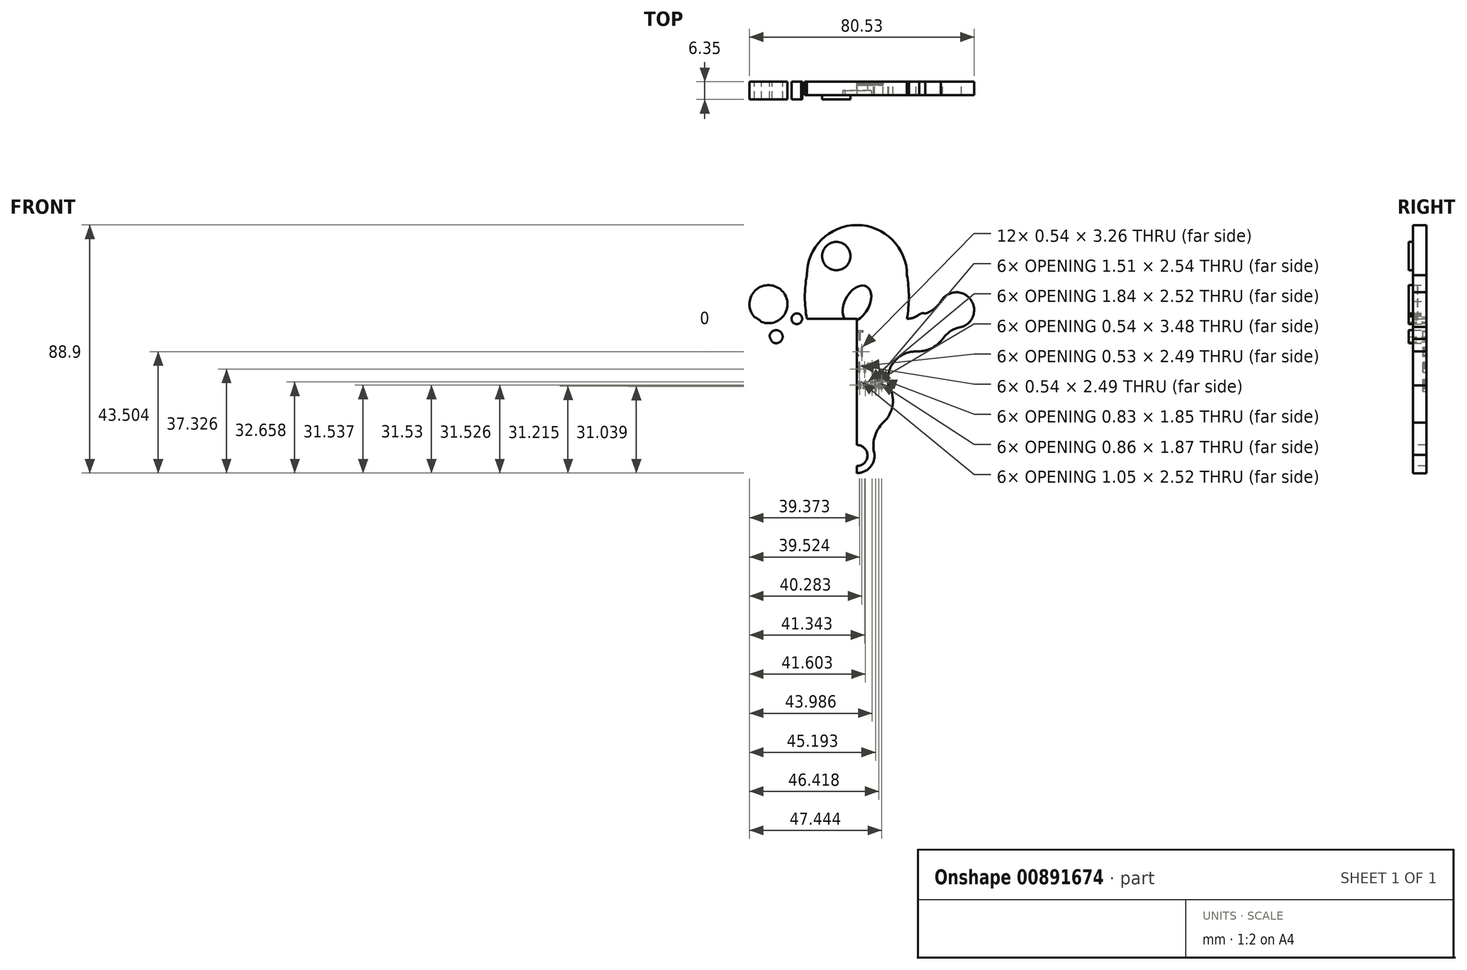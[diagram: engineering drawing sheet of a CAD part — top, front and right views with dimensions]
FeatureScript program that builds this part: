
annotation { "Feature Type Name" : "Feature", "Feature Type Description" : "" }
export const myFeature = defineFeature(function(context is Context, id is Id, definition is map)
    precondition{}
    {
        {
            var Q0;
            Q0=qCreatedBy(makeId("Front.planeOp"),FACE);
            var sketch = newSketch(context, id + "F0", { "sketchPlane" : qUnion([Q0])});
            skLineSegment(sketch, "E0.bottom", {"start": v(-17.94, 11.59) * mm, "end": v(17.94, 11.59) * mm});
            skLineSegment(sketch, "E0.top", {"start": v(-17.94, 27.23) * mm, "end": v(17.94, 27.23) * mm});
            skPoint(sketch, "E0.middle", {"position": v(0, 19.41) * mm});
            skArc(sketch, "E1", {"start": v(17.94, 27.23) * mm, "mid": v(0, 45.18) * mm, "end": v(-17.94, 27.23) * mm});
            skLineSegment(sketch, "E2", {"start": v(-17.94, 11.59) * mm, "end": v(0, 11.59) * mm});
            skLineSegment(sketch, "E3", {"start": v(0, 11.59) * mm, "end": v(0, -27.44) * mm});
            skLineSegment(sketch, "E4", {"start": v(0, -27.44) * mm, "end": v(0, -34) * mm});
            skCircle(sketch, "E5", {"center": v(-31.7, 16.82) * mm, "radius": 6.82 * mm});
            skCircle(sketch, "E6", {"center": v(35.65, 14.71) * mm, "radius": 6.36 * mm});
            skCircle(sketch, "E7", {"center": v(0, -37.4) * mm, "radius": 6.33 * mm});
            skCircle(sketch, "E8", {"center": v(-28.95, 5.17) * mm, "radius": 2.34 * mm});
            skCircle(sketch, "E9", {"center": v(-21.53, 11.59) * mm, "radius": 1.9 * mm});
            skArc(sketch, "E10", {"start": v(-19.98, 12.7) * mm, "mid": v(-19.1, 11.88) * mm, "end": v(-17.94, 11.59) * mm});
            skArc(sketch, "E11", {"start": v(-25.07, 18.4) * mm, "mid": v(-23.74, 15.74) * mm, "end": v(-21.82, 13.47) * mm});
            skArc(sketch, "E12", {"start": v(-6.2, -36.14) * mm, "mid": v(-8.21, -28.4) * mm, "end": v(-14.49, -23.44) * mm});
            skArc(sketch, "E13", {"start": v(-31.29, 5.17) * mm, "mid": v(-29.02, 1.8) * mm, "end": v(-25.38, 0) * mm});
            skPoint(sketch, "E14.startSnap0", {"position": v(10.2, -17.56) * mm});
            skArc(sketch, "E15", {"start": v(21.15, -0.12) * mm, "mid": v(13.28, -3.81) * mm, "end": v(11.38, -12.3) * mm});
            skArc(sketch, "E16", {"start": v(21.15, -0.12) * mm, "mid": v(26.51, 0.92) * mm, "end": v(30.77, 4.35) * mm});
            skCircle(sketch, "E17", {"center": v(23.71, 11.2) * mm, "radius": 2.37 * mm});
            skArc(sketch, "E18", {"start": v(24.52, 13.44) * mm, "mid": v(27.64, 15.17) * mm, "end": v(30.08, 17.78) * mm});
            skArc(sketch, "E19", {"start": v(17.94, 11.59) * mm, "mid": v(20.27, 11.99) * mm, "end": v(22.33, 13.14) * mm});
            skArc(sketch, "E20", {"start": v(37.47, 8.62) * mm, "mid": v(33.64, 7.23) * mm, "end": v(30.77, 4.35) * mm});
            skArc(sketch, "E21", {"start": v(-17.94, 27.23) * mm, "mid": v(-18.64, 19.41) * mm, "end": v(-17.94, 11.59) * mm});
            skArc(sketch, "E22", {"start": v(17.94, 11.59) * mm, "mid": v(18.6, 19.41) * mm, "end": v(17.94, 27.23) * mm});
            skArc(sketch, "E23", {"start": v(-20.49, -14.03) * mm, "mid": v(-19.15, -19.8) * mm, "end": v(-14.49, -23.44) * mm});
            skArc(sketch, "E24", {"start": v(-20.49, -14.03) * mm, "mid": v(-19.5, -5.82) * mm, "end": v(-25.38, 0) * mm});
            skArc(sketch, "E25", {"start": v(-31.29, 5.17) * mm, "mid": v(-33.14, 9.34) * mm, "end": v(-36.7, 12.19) * mm});
            skArc(sketch, "E26", {"start": v(9.44, -25.57) * mm, "mid": v(12.8, -19.28) * mm, "end": v(11.38, -12.3) * mm});
            skArc(sketch, "E27", {"start": v(9.44, -25.57) * mm, "mid": v(6.3, -30.92) * mm, "end": v(6.33, -37.12) * mm});
            skLineSegment(sketch, "E28", {"start": v(0, 45.18) * mm, "end": v(0, -43.72) * mm});
            skSolve(sketch);
        }
        {
            var Q0;
            Q0=makeQuery(id+"F0.imprint","IMPRINT",FACE,{"disambiguationData":[TD([[makeQuery(id+"F0.imprint","IMPRINT",EDGE,{"derivedFrom":sQuery(id+"F0.wireOp",EDGE,"E0.top")}),1.0]])]});
            var Q1;
            Q1=makeQuery(id+"F0.imprint","IMPRINT",FACE,{"disambiguationData":[TD([[makeQuery(id+"F0.imprint","IMPRINT",EDGE,{"derivedFrom":sQuery(id+"F0.wireOp",EDGE,"E0.bottom")}),1.0]])]});
            var Q2;
            {var subQ3=sQuery(id+"F0.wireOp",EDGE,"E2");Q2=makeQuery(id+"F0.imprint","IMPRINT",FACE,{"disambiguationData":[TD([[makeQuery(id+"F0.imprint","IMPRINT",EDGE,{"derivedFrom":subQ3}),-1.0]])]});}
            var Q3;
            {var subQ0=sQuery(id+"F0.wireOp",EDGE,"E5");var subQ1=makeQuery(id+"F0.imprint","INTERSECT",VERTEX,{"derivedFrom":[subQ0,sQuery(id+"F0.wireOp",EDGE,"E11")]});Q3=makeQuery(id+"F0.imprint","IMPRINT",FACE,{"disambiguationData":[TD([[makeQuery(id+"F0.imprint","IMPRINT",EDGE,{"disambiguationData":[TD([[subQ1,-1.0]])],"derivedFrom":subQ0}),1.0]])]});}
            var Q4;
            {var subQ12=sQuery(id+"F0.wireOp",EDGE,"E0.bottom");Q4=makeQuery(id+"F0.imprint","IMPRINT",FACE,{"disambiguationData":[TD([[makeQuery(id+"F0.imprint","IMPRINT",EDGE,{"derivedFrom":subQ12}),-1.0]])]});}
            var Q5;
            {var subQ0=sQuery(id+"F0.wireOp",EDGE,"E6");var subQ1=makeQuery(id+"F0.imprint","INTERSECT",VERTEX,{"derivedFrom":[subQ0,sQuery(id+"F0.wireOp",EDGE,"E18")]});Q5=makeQuery(id+"F0.imprint","IMPRINT",FACE,{"disambiguationData":[TD([[makeQuery(id+"F0.imprint","IMPRINT",EDGE,{"disambiguationData":[TD([[subQ1,-1.0]])],"derivedFrom":subQ0}),1.0]])]});}
            var Q6;
            {var subQ0=sQuery(id+"F0.wireOp",EDGE,"E17");var subQ1=makeQuery(id+"F0.imprint","INTERSECT",VERTEX,{"derivedFrom":[subQ0,sQuery(id+"F0.wireOp",EDGE,"E18")]});Q6=makeQuery(id+"F0.imprint","IMPRINT",FACE,{"disambiguationData":[TD([[makeQuery(id+"F0.imprint","IMPRINT",EDGE,{"disambiguationData":[TD([[subQ1,-1.0]])],"derivedFrom":subQ0}),1.0]])]});}
            var Q7;
            {var subQ0=sQuery(id+"F0.wireOp",EDGE,"E10");var subQ1=sQuery(id+"F0.wireOp",EDGE,"E9");var subQ2=makeQuery(id+"F0.imprint","INTERSECT",VERTEX,{"disambiguationData":[OD(0.0)],"derivedFrom":[subQ1,subQ0]});Q7=makeQuery(id+"F0.imprint","IMPRINT",FACE,{"disambiguationData":[TD([[makeQuery(id+"F0.imprint","IMPRINT",EDGE,{"disambiguationData":[TD([[subQ2,-1.0]])],"derivedFrom":subQ1}),1.0]])]});}
            var Q8;
            {var subQ0=sQuery(id+"F0.wireOp",EDGE,"E13");var subQ1=sQuery(id+"F0.wireOp",EDGE,"E8");var subQ3=makeQuery(id+"F0.imprint","INTERSECT",VERTEX,{"derivedFrom":[subQ1,subQ0]});Q8=makeQuery(id+"F0.imprint","IMPRINT",FACE,{"disambiguationData":[TD([[makeQuery(id+"F0.imprint","IMPRINT",EDGE,{"disambiguationData":[TD([[subQ3,-1.0]])],"derivedFrom":subQ1}),1.0]])]});}
            var Q9;
            {var subQ0=sQuery(id+"F0.wireOp",EDGE,"E7");var subQ1=makeQuery(id+"F0.imprint","INTERSECT",VERTEX,{"derivedFrom":[sQuery(id+"F0.wireOp",EDGE,"E4"),subQ0]});Q9=makeQuery(id+"F0.imprint","IMPRINT",FACE,{"disambiguationData":[TD([[makeQuery(id+"F0.imprint","IMPRINT",EDGE,{"disambiguationData":[TD([[subQ1,1.0]])],"derivedFrom":subQ0}),1.0]])]});}
            var Q10;
            {var subQ0=sQuery(id+"F0.wireOp",EDGE,"E28");var subQ1=makeQuery(id+"F0.imprint","IMPRINT",VERTEX,{"derivedFrom":subQ0});Q10=makeQuery(id+"F0.imprint","IMPRINT",FACE,{"disambiguationData":[TD([[makeQuery(id+"F0.imprint","IMPRINT",EDGE,{"disambiguationData":[TD([[subQ1,1.0]])],"derivedFrom":subQ0}),1.0]])]});}
            var Q11;
            {var subQ4=sQuery(id+"F0.wireOp",EDGE,"E2");Q11=makeQuery(id+"F0.imprint","IMPRINT",FACE,{"disambiguationData":[TD([[makeQuery(id+"F0.imprint","IMPRINT",EDGE,{"derivedFrom":subQ4}),1.0]])]});}
            extrude(context, id + "F1", {"entities" : qUnion([Q0, Q1, Q2, Q3, Q4, Q5, Q6, Q7, Q8, Q9, Q10, Q11]), "depth" : 6.35 * mm, "offsetDistance" : 25.4 * mm});
        }
        {
            var Q0;
            Q0=makeQuery(id+"F1.opExtrude","CAP_FACE",FACE,{"disambiguationData":[OSD([sQuery(id+"F0.wireOp",EDGE,"E1"),sQuery(id+"F0.wireOp",EDGE,"E5"),sQuery(id+"F0.wireOp",EDGE,"E6"),sQuery(id+"F0.wireOp",EDGE,"E7"),sQuery(id+"F0.wireOp",EDGE,"E9"),sQuery(id+"F0.wireOp",EDGE,"E10"),sQuery(id+"F0.wireOp",EDGE,"E11"),sQuery(id+"F0.wireOp",EDGE,"E12"),sQuery(id+"F0.wireOp",EDGE,"E13"),sQuery(id+"F0.wireOp",EDGE,"E15"),sQuery(id+"F0.wireOp",EDGE,"E16"),sQuery(id+"F0.wireOp",EDGE,"E17"),sQuery(id+"F0.wireOp",EDGE,"E18"),sQuery(id+"F0.wireOp",EDGE,"E19"),sQuery(id+"F0.wireOp",EDGE,"E20"),sQuery(id+"F0.wireOp",EDGE,"E21"),sQuery(id+"F0.wireOp",EDGE,"E22"),sQuery(id+"F0.wireOp",EDGE,"E23"),sQuery(id+"F0.wireOp",EDGE,"E24"),sQuery(id+"F0.wireOp",EDGE,"E25"),sQuery(id+"F0.wireOp",EDGE,"E26"),sQuery(id+"F0.wireOp",EDGE,"E27")])],"isStart":false});
            var sketch = newSketch(context, id + "F2", { "sketchPlane" : qUnion([Q0])});
            skCircle(sketch, "E29", {"center": v(7.39, 31.47) * mm, "radius": 5.22 * mm});
            skEllipse(sketch, "E30", {"center": v(0, 17.03) * mm, "majorRadius": 7.04 * mm, "minorRadius": 4.37 * mm, "majorAxis": v(-0.5, -0.87)});
            skCircle(sketch, "E31", {"center": v(-7.37, 34.04) * mm, "radius": 5.08 * mm});
            skCircle(sketch, "E32", {"center": v(0, -37.4) * mm, "radius": 3.64 * mm});
            skLineSegment(sketch, "E33", {"start": v(-7.37, 34.04) * mm, "end": v(0, 34.04) * mm});
            skLineSegment(sketch, "E34", {"start": v(7.39, 31.47) * mm, "end": v(0, 31.47) * mm});
            skPoint(sketch, "E34.endSnap0", {"position": v(0, 45.18) * mm});
            skLineSegment(sketch, "E35", {"start": v(0, 34.04) * mm, "end": v(0, 45.18) * mm});
            skLineSegment(sketch, "E36", {"start": v(0, 31.47) * mm, "end": v(0, 45.18) * mm});
            skSolve(sketch);
        }
        {
            var Q0;
            Q0=makeQuery(id+"F2.imprint","IMPRINT",FACE,{"disambiguationData":[TD([[makeQuery(id+"F2.imprint","IMPRINT",EDGE,{"derivedFrom":sQuery(id+"F2.wireOp",EDGE,"E30")}),1.0]])]});
            var Q1;
            Q1=sQuery(id+"F2.wireOp",EDGE,"E30");
            extrude(context, id + "F3", {"entities" : qUnion([Q0]), "operationType" : NewBodyOperationType.REMOVE, "surfaceEntities" : qUnion([Q1]), "oppositeDirection" : true, "depth" : 3.17 * mm, "offsetDistance" : 25.4 * mm});
        }
        {
            var Q0;
            Q0=makeQuery(id+"F1.opExtrude","CAP_FACE",FACE,{"disambiguationData":[OSD([sQuery(id+"F0.wireOp",EDGE,"E1"),sQuery(id+"F0.wireOp",EDGE,"E5"),sQuery(id+"F0.wireOp",EDGE,"E6"),sQuery(id+"F0.wireOp",EDGE,"E7"),sQuery(id+"F0.wireOp",EDGE,"E9"),sQuery(id+"F0.wireOp",EDGE,"E10"),sQuery(id+"F0.wireOp",EDGE,"E11"),sQuery(id+"F0.wireOp",EDGE,"E12"),sQuery(id+"F0.wireOp",EDGE,"E13"),sQuery(id+"F0.wireOp",EDGE,"E15"),sQuery(id+"F0.wireOp",EDGE,"E16"),sQuery(id+"F0.wireOp",EDGE,"E17"),sQuery(id+"F0.wireOp",EDGE,"E18"),sQuery(id+"F0.wireOp",EDGE,"E19"),sQuery(id+"F0.wireOp",EDGE,"E20"),sQuery(id+"F0.wireOp",EDGE,"E21"),sQuery(id+"F0.wireOp",EDGE,"E22"),sQuery(id+"F0.wireOp",EDGE,"E23"),sQuery(id+"F0.wireOp",EDGE,"E24"),sQuery(id+"F0.wireOp",EDGE,"E25"),sQuery(id+"F0.wireOp",EDGE,"E26"),sQuery(id+"F0.wireOp",EDGE,"E27")])],"isStart":false});
            var sketch = newSketch(context, id + "F4", { "sketchPlane" : qUnion([Q0])});
            skLineSegment(sketch, "E37", {"start": v(0, 45.18) * mm, "end": v(0, 34.03) * mm});
            skLineSegment(sketch, "E38", {"start": v(0, 34.03) * mm, "end": v(0, 45.18) * mm});
            skLineSegment(sketch, "E39", {"start": v(0, 45.18) * mm, "end": v(0, 31.46) * mm});
            skLineSegment(sketch, "E40", {"start": v(0, 34.03) * mm, "end": v(-7.37, 34.03) * mm});
            skLineSegment(sketch, "E41", {"start": v(0, 31.46) * mm, "end": v(7.37, 31.46) * mm});
            skCircle(sketch, "E42", {"center": v(-7.37, 34.03) * mm, "radius": 5.08 * mm});
            skCircle(sketch, "E43", {"center": v(7.37, 31.46) * mm, "radius": 5.22 * mm});
            skSolve(sketch);
        }
        {
            var Q0;
            Q0=makeQuery(id+"F4.imprint","IMPRINT",FACE,{"disambiguationData":[TD([[makeQuery(id+"F4.imprint","IMPRINT",EDGE,{"derivedFrom":sQuery(id+"F4.wireOp",EDGE,"E42")}),-1.0]])]});
            var Q1;
            Q1=makeQuery(id+"F4.imprint","IMPRINT",FACE,{"disambiguationData":[TD([[makeQuery(id+"F4.imprint","IMPRINT",EDGE,{"derivedFrom":sQuery(id+"F4.wireOp",EDGE,"E43")}),1.0]])]});
            extrude(context, id + "F5", {"entities" : qUnion([Q0, Q1]), "operationType" : NewBodyOperationType.REMOVE, "oppositeDirection" : true, "depth" : 1.59 * mm, "offsetDistance" : 25.4 * mm});
        }
        {
            var Q0;
            Q0=makeQuery(id+"F1.opExtrude","CAP_FACE",FACE,{"disambiguationData":[OSD([sQuery(id+"F0.wireOp",EDGE,"E1"),sQuery(id+"F0.wireOp",EDGE,"E5"),sQuery(id+"F0.wireOp",EDGE,"E6"),sQuery(id+"F0.wireOp",EDGE,"E7"),sQuery(id+"F0.wireOp",EDGE,"E9"),sQuery(id+"F0.wireOp",EDGE,"E10"),sQuery(id+"F0.wireOp",EDGE,"E11"),sQuery(id+"F0.wireOp",EDGE,"E12"),sQuery(id+"F0.wireOp",EDGE,"E13"),sQuery(id+"F0.wireOp",EDGE,"E15"),sQuery(id+"F0.wireOp",EDGE,"E16"),sQuery(id+"F0.wireOp",EDGE,"E17"),sQuery(id+"F0.wireOp",EDGE,"E18"),sQuery(id+"F0.wireOp",EDGE,"E19"),sQuery(id+"F0.wireOp",EDGE,"E20"),sQuery(id+"F0.wireOp",EDGE,"E21"),sQuery(id+"F0.wireOp",EDGE,"E22"),sQuery(id+"F0.wireOp",EDGE,"E23"),sQuery(id+"F0.wireOp",EDGE,"E24"),sQuery(id+"F0.wireOp",EDGE,"E25"),sQuery(id+"F0.wireOp",EDGE,"E26"),sQuery(id+"F0.wireOp",EDGE,"E27")])],"isStart":false});
            var sketch = newSketch(context, id + "F6", { "sketchPlane" : qUnion([Q0])});
            skCircle(sketch, "E44", {"center": v(0, -37.4) * mm, "radius": 3.77 * mm});
            skSolve(sketch);
        }
        {
            var Q0;
            Q0=makeQuery(id+"F6.imprint","IMPRINT",FACE,{"disambiguationData":[TD([[makeQuery(id+"F6.imprint","IMPRINT",EDGE,{"derivedFrom":sQuery(id+"F6.wireOp",EDGE,"E44")}),1.0]])]});
            extrude(context, id + "F7", {"entities" : qUnion([Q0]), "operationType" : NewBodyOperationType.REMOVE, "oppositeDirection" : true, "depth" : 25.4 * mm, "offsetDistance" : 25.4 * mm});
        }
        {
            var Q0;
            Q0=makeQuery(id+"F1.opExtrude","CAP_FACE",FACE,{"disambiguationData":[OSD([sQuery(id+"F0.wireOp",EDGE,"E1"),sQuery(id+"F0.wireOp",EDGE,"E5"),sQuery(id+"F0.wireOp",EDGE,"E6"),sQuery(id+"F0.wireOp",EDGE,"E7"),sQuery(id+"F0.wireOp",EDGE,"E9"),sQuery(id+"F0.wireOp",EDGE,"E10"),sQuery(id+"F0.wireOp",EDGE,"E11"),sQuery(id+"F0.wireOp",EDGE,"E12"),sQuery(id+"F0.wireOp",EDGE,"E13"),sQuery(id+"F0.wireOp",EDGE,"E15"),sQuery(id+"F0.wireOp",EDGE,"E16"),sQuery(id+"F0.wireOp",EDGE,"E17"),sQuery(id+"F0.wireOp",EDGE,"E18"),sQuery(id+"F0.wireOp",EDGE,"E19"),sQuery(id+"F0.wireOp",EDGE,"E20"),sQuery(id+"F0.wireOp",EDGE,"E21"),sQuery(id+"F0.wireOp",EDGE,"E22"),sQuery(id+"F0.wireOp",EDGE,"E23"),sQuery(id+"F0.wireOp",EDGE,"E24"),sQuery(id+"F0.wireOp",EDGE,"E25"),sQuery(id+"F0.wireOp",EDGE,"E26"),sQuery(id+"F0.wireOp",EDGE,"E27")])],"isStart":true});
            var sketch = newSketch(context, id + "F8", { "sketchPlane" : qUnion([Q0])});
            skText(sketch, "E45", { "text": "      The \n      ISS\'s\n   Friendly\nSpace Ghost", "fontName": "AllertaStencil-Regular.ttf"});
            const initialGuessF8  = {"E45": [-0.00972, 0.00395, 1, 0, 0.00326]};
            skSetInitialGuess(sketch, initialGuessF8);
            skSolve(sketch);
        }
        {
            var Q0;
            Q0 = qSketchRegion(id + "F8", true);
            extrude(context, id + "F9", {"entities" : qUnion([Q0]), "operationType" : NewBodyOperationType.REMOVE, "oppositeDirection" : true, "depth" : 1.27 * mm, "offsetDistance" : 25.4 * mm});
        }
    });
